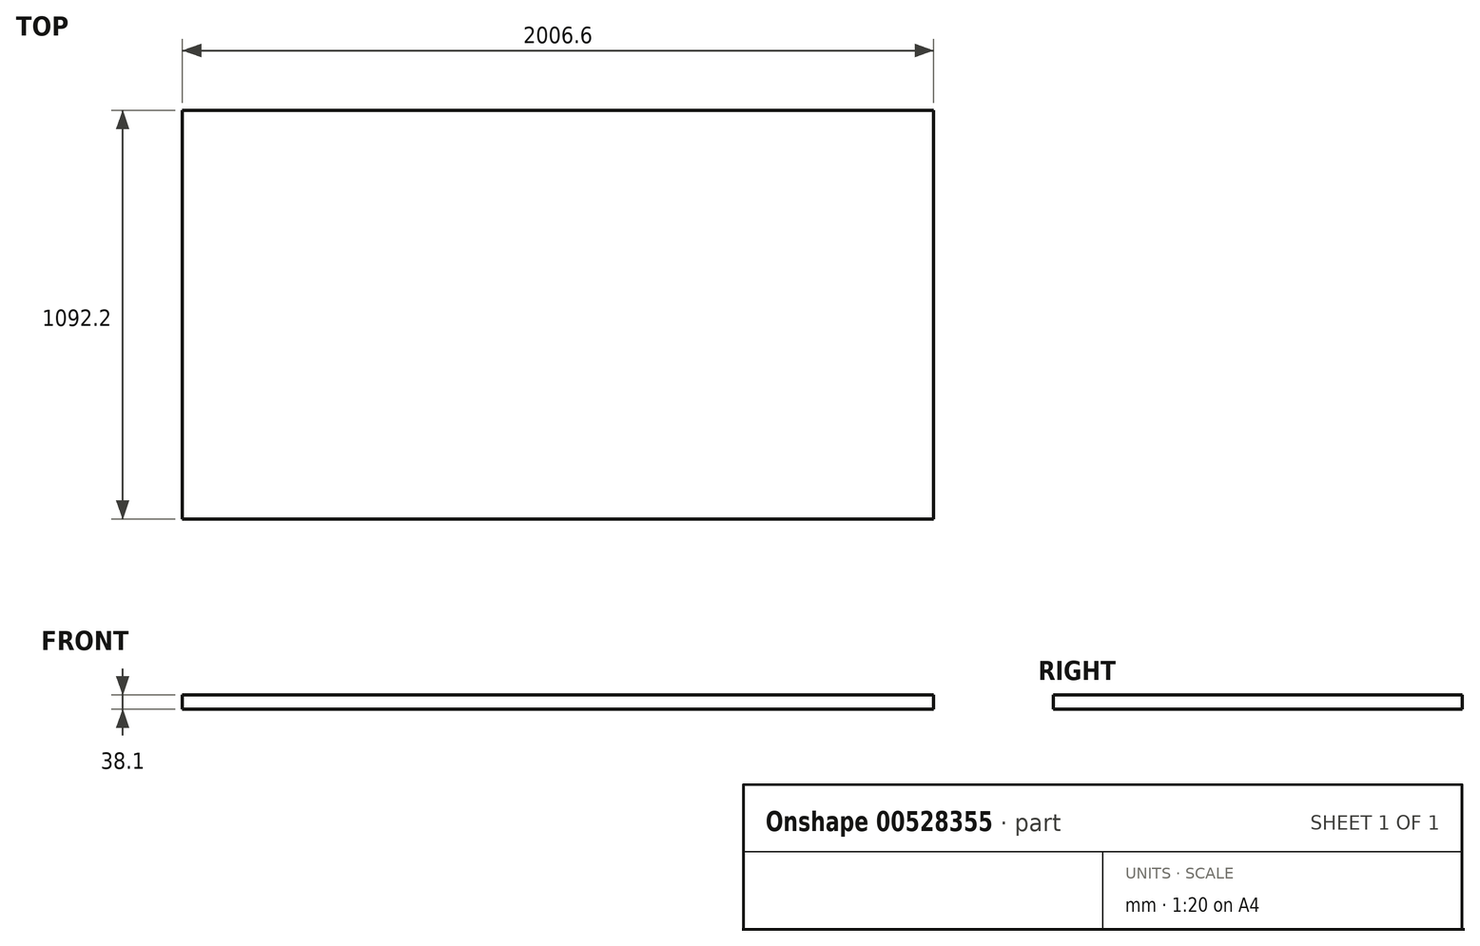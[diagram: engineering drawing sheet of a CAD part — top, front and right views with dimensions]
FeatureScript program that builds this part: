
annotation { "Feature Type Name" : "Feature", "Feature Type Description" : "" }
export const myFeature = defineFeature(function(context is Context, id is Id, definition is map)
    precondition{}
    {
        {
            var Q0;
            Q0=qCreatedBy(makeId("Top.planeOp"),FACE);
            var sketch = newSketch(context, id + "F0", { "sketchPlane" : qUnion([Q0])});
            skLineSegment(sketch, "E0.bottom", {"start": v(-116.84, 63.1) * mm, "end": v(1889.76, 63.1) * mm});
            skLineSegment(sketch, "E0.top", {"start": v(-116.84, -1029.1) * mm, "end": v(1889.76, -1029.1) * mm});
            skLineSegment(sketch, "E0.left", {"start": v(-116.84, 63.1) * mm, "end": v(-116.84, -1029.1) * mm});
            skLineSegment(sketch, "E0.right", {"start": v(1889.76, 63.1) * mm, "end": v(1889.76, -1029.1) * mm});
            skSolve(sketch);
        }
        {
            var Q0;
            Q0=makeQuery(id+"F0.imprint","IMPRINT",FACE,{"disambiguationData":[TD([[makeQuery(id+"F0.imprint","IMPRINT",EDGE,{"derivedFrom":sQuery(id+"F0.wireOp",EDGE,"E0.bottom")}),-1.0]])]});
            extrude(context, id + "F1", {"entities" : qUnion([Q0]), "depth" : 38.1 * mm, "offsetDistance" : 25.4 * mm});
        }
    });
